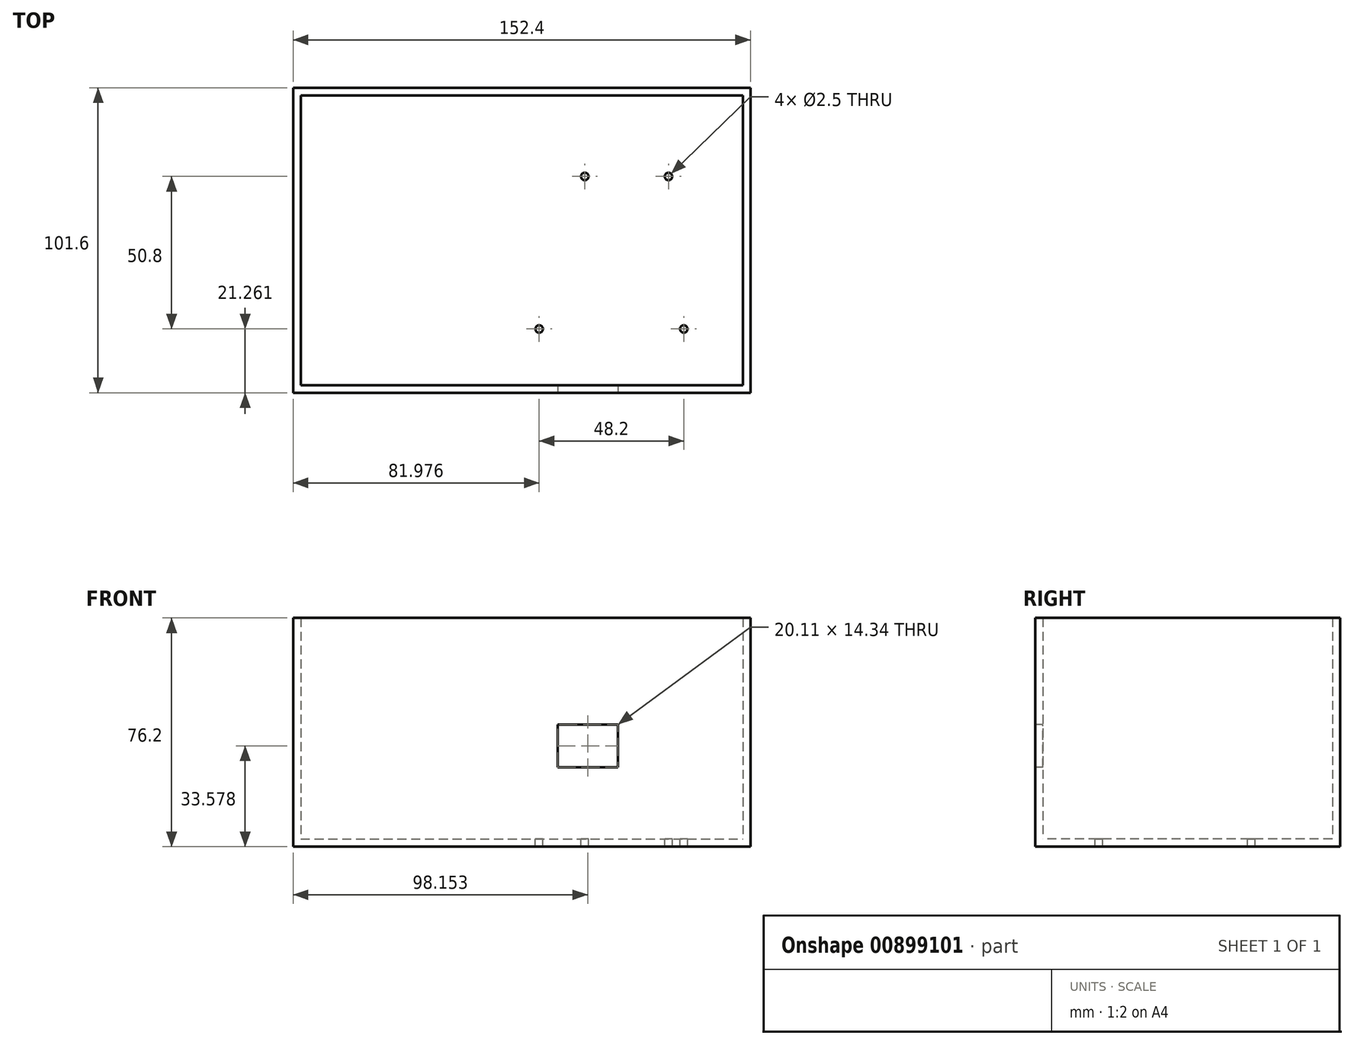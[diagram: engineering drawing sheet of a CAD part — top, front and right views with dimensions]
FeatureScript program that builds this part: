
annotation { "Feature Type Name" : "Feature", "Feature Type Description" : "" }
export const myFeature = defineFeature(function(context is Context, id is Id, definition is map)
    precondition{}
    {
        {
            var Q0;
            Q0=qCreatedBy(makeId("Top.planeOp"),FACE);
            var sketch = newSketch(context, id + "F0", { "sketchPlane" : qUnion([Q0])});
            skLineSegment(sketch, "E0.bottom", {"start": v(-60.64, 56.03) * mm, "end": v(91.76, 56.03) * mm});
            skLineSegment(sketch, "E0.top", {"start": v(-60.64, -45.57) * mm, "end": v(91.76, -45.57) * mm});
            skLineSegment(sketch, "E0.left", {"start": v(-60.64, 56.03) * mm, "end": v(-60.64, -45.57) * mm});
            skLineSegment(sketch, "E0.right", {"start": v(91.76, 56.03) * mm, "end": v(91.76, -45.57) * mm});
            skSolve(sketch);
        }
        {
            var Q0;
            Q0=makeQuery(id+"F0.imprint","IMPRINT",FACE,{"disambiguationData":[TD([[makeQuery(id+"F0.imprint","IMPRINT",EDGE,{"derivedFrom":sQuery(id+"F0.wireOp",EDGE,"E0.bottom")}),-1.0]])]});
            extrude(context, id + "F1", {"entities" : qUnion([Q0]), "depth" : 76.2 * mm, "offsetDistance" : 25.4 * mm});
        }
        {
            var Q0;
            Q0=makeQuery(id+"F1.opExtrude","CAP_FACE",FACE,{"disambiguationData":[OSD([sQuery(id+"F0.wireOp",EDGE,"E0.bottom"),sQuery(id+"F0.wireOp",EDGE,"E0.top"),sQuery(id+"F0.wireOp",EDGE,"E0.left"),sQuery(id+"F0.wireOp",EDGE,"E0.right")])],"isStart":false});
            shell(context, id + "F2", {"entities" : qUnion([Q0]), "thickness" : 2.54 * mm});
        }
        {
            var Q0;
            Q0=makeQuery(id+"F2.opShell","OFFSET_FACE",FACE,{"disambiguationData":[OSD([sQuery(id+"F0.wireOp",EDGE,"E0.bottom"),sQuery(id+"F0.wireOp",EDGE,"E0.top"),sQuery(id+"F0.wireOp",EDGE,"E0.left"),sQuery(id+"F0.wireOp",EDGE,"E0.right")])]});
            var sketch = newSketch(context, id + "F3", { "sketchPlane" : qUnion([Q0])});
            skPoint(sketch, "E1", {"position": v(21.34, -24.3) * mm});
            skPoint(sketch, "E2", {"position": v(64.44, 26.5) * mm});
            skPoint(sketch, "E3", {"position": v(36.54, 26.5) * mm});
            skPoint(sketch, "E4", {"position": v(69.54, -24.3) * mm});
            skCircle(sketch, "E5", {"center": v(21.34, -24.3) * mm, "radius": 1.25 * mm});
            skCircle(sketch, "E6", {"center": v(36.54, 26.5) * mm, "radius": 1.25 * mm});
            skCircle(sketch, "E7", {"center": v(64.44, 26.5) * mm, "radius": 1.25 * mm});
            skCircle(sketch, "E8", {"center": v(69.54, -24.3) * mm, "radius": 1.25 * mm});
            skSolve(sketch);
        }
        {
            var Q0;
            Q0 = qSketchRegion(id + "F3", true);
            extrude(context, id + "F4", {"entities" : qUnion([Q0]), "operationType" : NewBodyOperationType.REMOVE, "endBound" : BoundingType.THROUGH_ALL, "oppositeDirection" : true, "depth" : 25.4 * mm, "offsetDistance" : 25.4 * mm});
        }
        {
            var Q0;
            Q0=makeQuery(id+"F1.opExtrude","SWEPT_FACE",FACE,{"disambiguationData":[OSD([sQuery(id+"F0.wireOp",EDGE,"E0.top")])]});
            var sketch = newSketch(context, id + "F5", { "sketchPlane" : qUnion([Q0])});
            skLineSegment(sketch, "E9.bottom", {"start": v(27.46, 40.75) * mm, "end": v(47.57, 40.75) * mm});
            skLineSegment(sketch, "E9.top", {"start": v(27.46, 26.4) * mm, "end": v(47.57, 26.4) * mm});
            skLineSegment(sketch, "E9.left", {"start": v(27.46, 40.75) * mm, "end": v(27.46, 26.4) * mm});
            skLineSegment(sketch, "E9.right", {"start": v(47.57, 40.75) * mm, "end": v(47.57, 26.4) * mm});
            skSolve(sketch);
        }
        {
            var Q0;
            Q0 = qSketchRegion(id + "F5", true);
            extrude(context, id + "F6", {"entities" : qUnion([Q0]), "operationType" : NewBodyOperationType.REMOVE, "oppositeDirection" : true, "depth" : 25.4 * mm, "offsetDistance" : 25.4 * mm});
        }
    });
